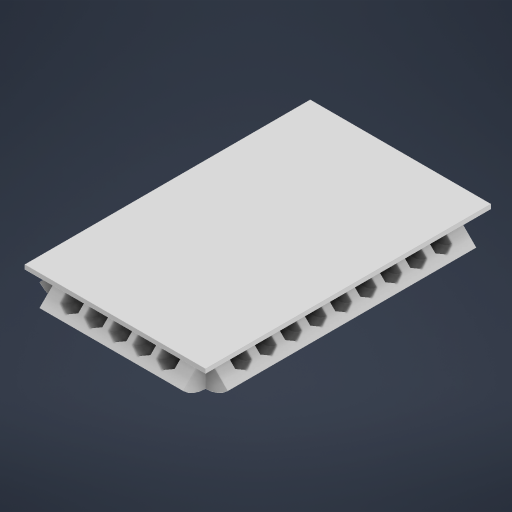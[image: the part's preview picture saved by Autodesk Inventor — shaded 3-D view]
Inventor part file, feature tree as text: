
AUTODESK INVENTOR PART (.ipt)
format: ipt  version: 2023 (Build 270158000, 158)  size: 1,201,664 bytes
history: native  units: mm
features: sketch x12, extrude x10, revolve x3, shell x1
ambient origin geometry x8: Origin, YZ Plane, XZ Plane, XY Plane, X Axis, Y Axis, Z Axis, Center Point
bodies: Solid1 (feature_tree)
feature tree (26):
  sketch  "Sketch1"  dims[d0=77.5mm d1=134.0mm]
  extrude  "Extrusion1"  Depth=134.0mm
  extrude  "Extrusion2"  Depth=5.0mm
  shell  "Shell1"  Thickness=5.0mm
  extrude  "Extrusion3"  Depth=3.0mm TaperAngle=0.0deg
  extrude  "Extrusion4"  Depth=4.0mm
  extrude  "Extrusion5"  Depth=4.0mm
  extrude  "Extrusion6"  Depth=8.0mm
  extrude  "Extrusion7"  Depth=4.0mm TaperAngle=0.0deg
  extrude  "Extrusion8"  Depth=0.3mm TaperAngle=0.0deg
  extrude  "Extrusion9"  Depth=5.0mm
  extrude  "Extrusion10"  Depth=5.0mm
  revolve  "Revolution1"  [1 undecoded]
  sketch  "Sketch11"  dims[d35=5.0mm d36=2.3mm d37=0.0mm]
  revolve  "Revolution2"  [1 undecoded]
  revolve  "Revolution3"  [1 undecoded]
  sketch  "Sketch2"  dims[d2=5.0mm d3=5.0mm d4=5.0mm]
  sketch  "Sketch3"  dims[d5=5.0mm d6=3.0mm d7=0.0mm]
  sketch  "Sketch4"  dims[d8=2.0mm d9=0.0mm d10=4.0mm]
  sketch  "Sketch5"  dims[d11=1.0mm d12=0.0mm d13=4.0mm]
  sketch  "Sketch6"  dims[d14=1.0mm d15=8.0mm]
  sketch  "Sketch7"  dims[d16=100.0mm d18=12.0mm d19=60.0mm d21=12.0mm d24=4.0mm d25=0.0mm]
  sketch  "Sketch8"  dims[d26=4.0mm d27=0.0mm d28=0.3mm d29=0.0mm]
  sketch  "Sketch9"  dims[d30=10.0mm d31=0.0mm d32=5.0mm]
  sketch  "Sketch10"  dims[d33=5.0mm d34=5.0mm]
  sketch  "Sketch12"  dims[d38=90.0mm d40=13.5mm d41=10.0mm d43=10.0mm d45=222.0mm d46=0.0mm d47=50.0mm d49=13.0mm d50=10.0mm d52=10.0mm d54=222.0mm d55=0.0mm d56=45.0deg d57=45.0deg d58=45.0deg]
note: 3 required parameter values undecoded (feature->parameter linkage not recoverable at this tier; creation-order binding heuristic only, values carry confidence <= 0.55)
